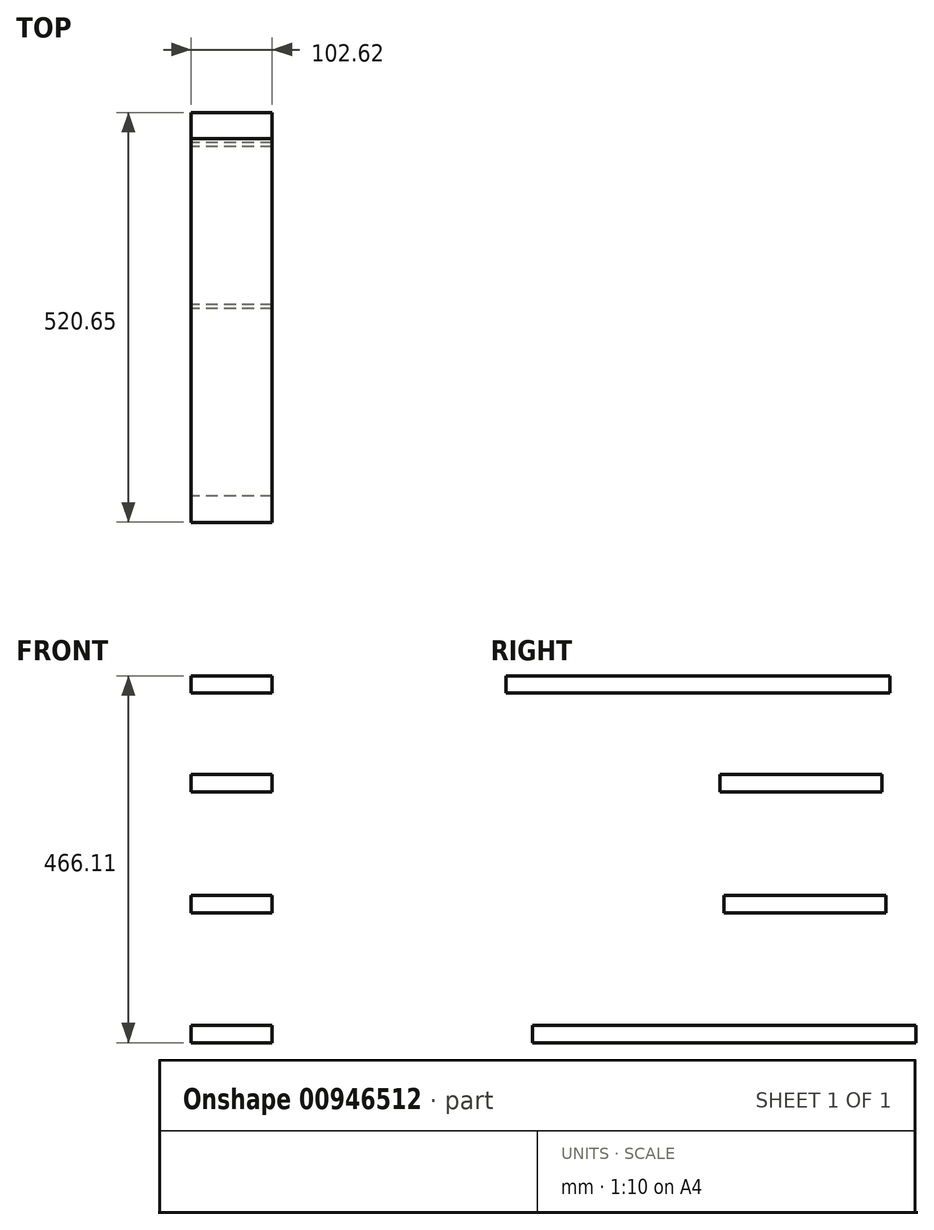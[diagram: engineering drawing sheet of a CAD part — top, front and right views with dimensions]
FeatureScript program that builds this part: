
annotation { "Feature Type Name" : "Feature", "Feature Type Description" : "" }
export const myFeature = defineFeature(function(context is Context, id is Id, definition is map)
    precondition{}
    {
        {
            var Q0;
            Q0=qCreatedBy(makeId("Right.planeOp"),FACE);
            var sketch = newSketch(context, id + "F0", { "sketchPlane" : qUnion([Q0])});
            skLineSegment(sketch, "E0.bottom", {"start": v(-128.93, 42.4) * mm, "end": v(-616.35, 42.4) * mm});
            skLineSegment(sketch, "E0.top", {"start": v(-128.93, 20.3) * mm, "end": v(-616.35, 20.3) * mm});
            skLineSegment(sketch, "E0.left", {"start": v(-128.93, 42.4) * mm, "end": v(-128.93, 20.3) * mm});
            skLineSegment(sketch, "E0.right", {"start": v(-616.35, 42.4) * mm, "end": v(-616.35, 20.3) * mm});
            skLineSegment(sketch, "E1.bottom", {"start": v(-139.43, -82.95) * mm, "end": v(-344.66, -82.95) * mm});
            skLineSegment(sketch, "E1.top", {"start": v(-139.43, -105.05) * mm, "end": v(-344.66, -105.05) * mm});
            skLineSegment(sketch, "E1.left", {"start": v(-139.43, -82.95) * mm, "end": v(-139.43, -105.05) * mm});
            skLineSegment(sketch, "E1.right", {"start": v(-344.66, -82.95) * mm, "end": v(-344.66, -105.05) * mm});
            skLineSegment(sketch, "E2.bottom", {"start": v(-134.31, -236.85) * mm, "end": v(-339.54, -236.85) * mm});
            skLineSegment(sketch, "E2.top", {"start": v(-134.31, -258.95) * mm, "end": v(-339.54, -258.95) * mm});
            skLineSegment(sketch, "E2.left", {"start": v(-134.31, -236.85) * mm, "end": v(-134.31, -258.95) * mm});
            skLineSegment(sketch, "E2.right", {"start": v(-339.54, -236.85) * mm, "end": v(-339.54, -258.95) * mm});
            skLineSegment(sketch, "E3.bottom", {"start": v(-95.7, -401.6) * mm, "end": v(-583.13, -401.6) * mm});
            skLineSegment(sketch, "E3.top", {"start": v(-95.7, -423.7) * mm, "end": v(-583.13, -423.7) * mm});
            skLineSegment(sketch, "E3.left", {"start": v(-95.7, -401.6) * mm, "end": v(-95.7, -423.7) * mm});
            skLineSegment(sketch, "E3.right", {"start": v(-583.13, -401.6) * mm, "end": v(-583.13, -423.7) * mm});
            skSolve(sketch);
        }
        {
            var Q0;
            Q0 = qSketchRegion(id + "F0", true);
            extrude(context, id + "F1", {"entities" : qUnion([Q0]), "depth" : 102.62 * mm, "offsetDistance" : 25.4 * mm});
        }
    });
